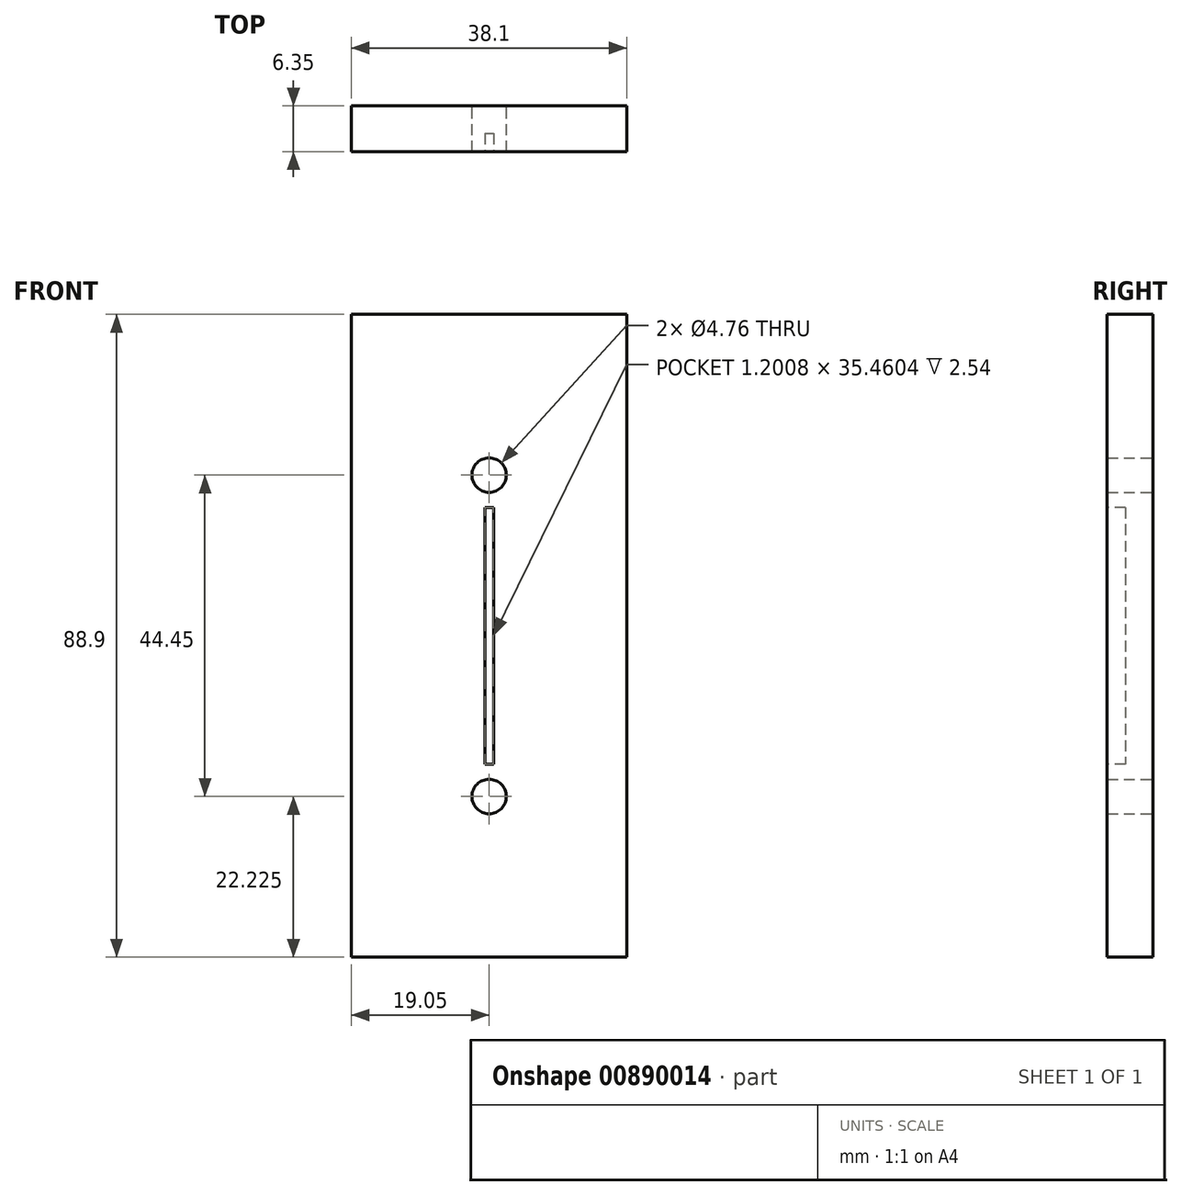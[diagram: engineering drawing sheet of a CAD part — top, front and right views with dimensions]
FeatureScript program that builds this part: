
annotation { "Feature Type Name" : "Feature", "Feature Type Description" : "" }
export const myFeature = defineFeature(function(context is Context, id is Id, definition is map)
    precondition{}
    {
        {
            var Q0;
            Q0=qCreatedBy(makeId("Front.planeOp"),FACE);
            var sketch = newSketch(context, id + "F0", { "sketchPlane" : qUnion([Q0])});
            skLineSegment(sketch, "E0.bottom", {"start": v(0, 0) * mm, "end": v(38.1, 0) * mm});
            skLineSegment(sketch, "E0.top", {"start": v(0, 88.9) * mm, "end": v(38.1, 88.9) * mm});
            skLineSegment(sketch, "E0.left", {"start": v(0, 0) * mm, "end": v(0, 88.9) * mm});
            skLineSegment(sketch, "E0.right", {"start": v(38.1, 0) * mm, "end": v(38.1, 88.9) * mm});
            skLineSegment(sketch, "E1", {"start": v(0, 44.45) * mm, "end": v(38.1, 44.45) * mm, "construction": true});
            skLineSegment(sketch, "E2", {"start": v(19.05, 44.45) * mm, "end": v(19.05, 88.9) * mm, "construction": true});
            skLineSegment(sketch, "E3", {"start": v(19.05, 44.45) * mm, "end": v(19.05, 0) * mm, "construction": true});
            skCircle(sketch, "E4", {"center": v(19.05, 22.23) * mm, "radius": 2.38 * mm});
            skCircle(sketch, "E5", {"center": v(19.05, 66.68) * mm, "radius": 2.38 * mm});
            skSolve(sketch);
        }
        {
            var Q0;
            Q0 = qSketchRegion(id + "F0", true);
            extrude(context, id + "F1", {"entities" : qUnion([Q0]), "depth" : 6.35 * mm, "offsetDistance" : 25.4 * mm});
        }
        {
            var Q0;
            Q0=makeQuery(id+"F1.opExtrude","CAP_FACE",FACE,{"disambiguationData":[OSD([sQuery(id+"F0.wireOp",EDGE,"E0.bottom"),sQuery(id+"F0.wireOp",EDGE,"E0.top"),sQuery(id+"F0.wireOp",EDGE,"E0.left"),sQuery(id+"F0.wireOp",EDGE,"E0.right"),sQuery(id+"F0.wireOp",EDGE,"E4"),sQuery(id+"F0.wireOp",EDGE,"E5")])],"isStart":false});
            var sketch = newSketch(context, id + "F2", { "sketchPlane" : qUnion([Q0])});
            skLineSegment(sketch, "E6", {"start": v(19.05, 22.23) * mm, "end": v(19.05, 66.68) * mm, "construction": true});
            skLineSegment(sketch, "E7.bottom", {"start": v(18.45, 62.18) * mm, "end": v(19.65, 62.18) * mm});
            skLineSegment(sketch, "E7.top", {"start": v(18.45, 26.72) * mm, "end": v(19.65, 26.72) * mm});
            skLineSegment(sketch, "E7.left", {"start": v(18.45, 62.18) * mm, "end": v(18.45, 26.72) * mm});
            skLineSegment(sketch, "E7.right", {"start": v(19.65, 62.18) * mm, "end": v(19.65, 26.72) * mm});
            skPoint(sketch, "E7.middle", {"position": v(19.05, 44.45) * mm});
            skSolve(sketch);
        }
        {
            var Q0;
            Q0 = qSketchRegion(id + "F2", true);
            extrude(context, id + "F3", {"entities" : qUnion([Q0]), "operationType" : NewBodyOperationType.REMOVE, "oppositeDirection" : true, "depth" : 2.54 * mm, "offsetDistance" : 25.4 * mm});
        }
    });
